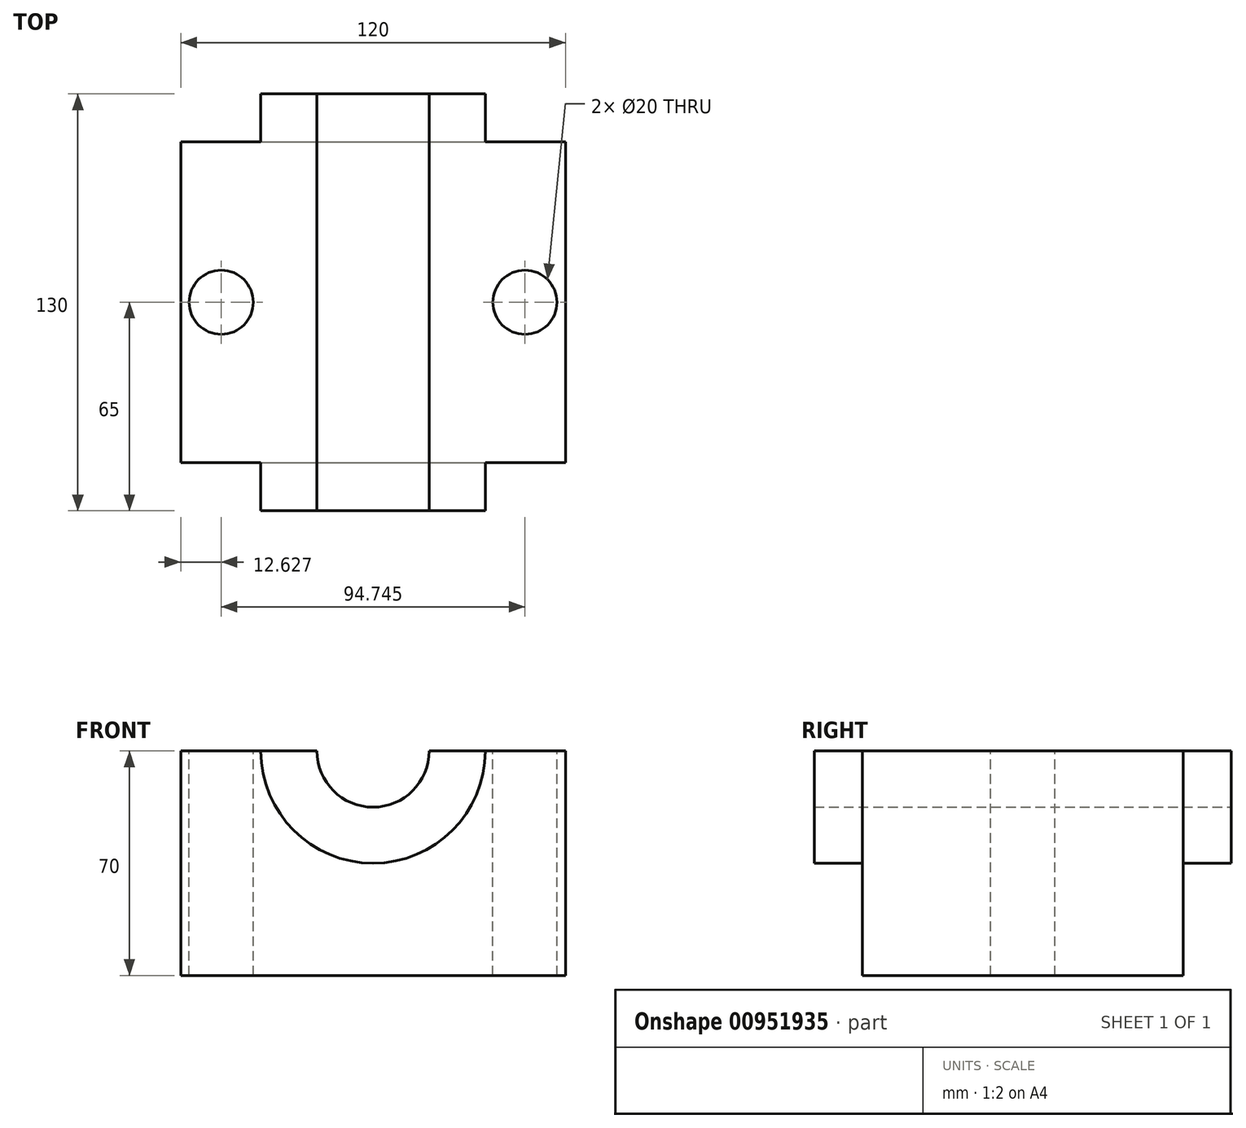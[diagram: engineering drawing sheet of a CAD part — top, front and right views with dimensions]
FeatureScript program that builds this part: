
annotation { "Feature Type Name" : "Feature", "Feature Type Description" : "" }
export const myFeature = defineFeature(function(context is Context, id is Id, definition is map)
    precondition{}
    {
        {
            var Q0;
            Q0=qCreatedBy(makeId("Front.planeOp"),FACE);
            var sketch = newSketch(context, id + "F0", { "sketchPlane" : qUnion([Q0])});
            skLineSegment(sketch, "E0.bottom", {"start": v(0, 35) * mm, "end": v(60, 35) * mm});
            skLineSegment(sketch, "E0.top", {"start": v(0, -35) * mm, "end": v(60, -35) * mm});
            skLineSegment(sketch, "E0.right", {"start": v(60, 35) * mm, "end": v(60, -35) * mm});
            skArc(sketch, "E1", {"start": v(0, 17.5) * mm, "mid": v(12.37, 22.63) * mm, "end": v(17.5, 35) * mm});
            skArc(sketch, "E2", {"start": v(0, 0) * mm, "mid": v(24.75, 10.25) * mm, "end": v(35, 35) * mm});
            skLineSegment(sketch, "E3", {"start": v(0, 35) * mm, "end": v(0, -35) * mm});
            skSolve(sketch);
        }
        {
            var Q0;
            Q0=makeQuery(id+"F0.imprint","IMPRINT",FACE,{"disambiguationData":[TD([[makeQuery(id+"F0.imprint","IMPRINT",EDGE,{"derivedFrom":sQuery(id+"F0.wireOp",EDGE,"E0.top")}),1.0]])]});
            extrude(context, id + "F1", {"entities" : qUnion([Q0]), "depth" : 50 * mm, "offsetDistance" : 25 * mm});
        }
        {
            var Q0;
            Q0=makeQuery(id+"F1.opExtrude","CAP_FACE",FACE,{"disambiguationData":[OSD([sQuery(id+"F0.wireOp",EDGE,"E0.bottom"),sQuery(id+"F0.wireOp",EDGE,"E0.top"),sQuery(id+"F0.wireOp",EDGE,"E0.left"),sQuery(id+"F0.wireOp",EDGE,"E0.right"),sQuery(id+"F0.wireOp",EDGE,"E2")])],"isStart":true});
            extrude(context, id + "F2", {"entities" : qUnion([Q0]), "operationType" : NewBodyOperationType.ADD, "depth" : 50 * mm, "offsetDistance" : 25 * mm});
        }
        {
            var Q0;
            {var subQ0=sQuery(id+"F0.wireOp",EDGE,"E1");Q0=makeQuery(id+"F0.imprint","IMPRINT",FACE,{"disambiguationData":[TD([[makeQuery(id+"F0.imprint","IMPRINT",EDGE,{"derivedFrom":subQ0}),-1.0]])]});}
            extrude(context, id + "F3", {"entities" : qUnion([Q0]), "operationType" : NewBodyOperationType.ADD, "depth" : 65 * mm, "offsetDistance" : 25 * mm});
        }
        {
            var Q0;
            Q0=makeQuery(id+"F3.opExtrude","CAP_FACE",FACE,{"disambiguationData":[OSD([sQuery(id+"F0.wireOp",EDGE,"E0.bottom"),sQuery(id+"F0.wireOp",EDGE,"E1"),sQuery(id+"F0.wireOp",EDGE,"E2")])],"isStart":true});
            extrude(context, id + "F4", {"entities" : qUnion([Q0]), "operationType" : NewBodyOperationType.ADD, "depth" : 65 * mm, "offsetDistance" : 25 * mm});
        }
        {
            var Q0;
            {var subQ0=sQuery(id+"F0.wireOp",EDGE,"E0.bottom");Q0=makeQuery(id+"F4.boolean.opBoolean","MERGE",FACE,{"derivedFrom":[makeQuery(id+"F3.boolean.opBoolean","MERGE",FACE,{"derivedFrom":[makeQuery(id+"F2.boolean.opBoolean","MERGE",FACE,{"derivedFrom":[makeQuery(id+"F1.opExtrude","SWEPT_FACE",FACE,{"disambiguationData":[OSD([subQ0])]}),makeQuery(id+"F2.opExtrude","SWEPT_FACE",FACE,{"disambiguationData":[OSD([subQ0])]})]}),makeQuery(id+"F3.opExtrude","SWEPT_FACE",FACE,{"disambiguationData":[OSD([subQ0])]})]}),makeQuery(id+"F4.opExtrude","SWEPT_FACE",FACE,{"disambiguationData":[OSD([subQ0])]})]});}
            var sketch = newSketch(context, id + "F5", { "sketchPlane" : qUnion([Q0])});
            skCircle(sketch, "E4", {"center": v(47.37, 0) * mm, "radius": 10 * mm});
            skSolve(sketch);
        }
        {
            var Q0;
            Q0=makeQuery(id+"F5.imprint","IMPRINT",FACE,{"disambiguationData":[TD([[makeQuery(id+"F5.imprint","IMPRINT",EDGE,{"derivedFrom":sQuery(id+"F5.wireOp",EDGE,"E4")}),1.0]])]});
            extrude(context, id + "F6", {"entities" : qUnion([Q0]), "operationType" : NewBodyOperationType.REMOVE, "oppositeDirection" : true, "depth" : 200 * mm, "offsetDistance" : 25 * mm});
        }
        {
            var Q0;
            Q0=makeQuery(id+"F1.opExtrude","SWEPT_BODY",BODY,{"disambiguationData":[OSD([sQuery(id+"F0.wireOp",EDGE,"E0.bottom"),sQuery(id+"F0.wireOp",EDGE,"E0.top"),sQuery(id+"F0.wireOp",EDGE,"E0.right"),sQuery(id+"F0.wireOp",EDGE,"E2"),sQuery(id+"F0.wireOp",EDGE,"E3")])]});
            var Q1;
            {var subQ0=sQuery(id+"F0.wireOp",EDGE,"E3");Q1=makeQuery(id+"F4.boolean.opBoolean","MERGE",FACE,{"derivedFrom":[makeQuery(id+"F3.boolean.opBoolean","MERGE",FACE,{"derivedFrom":[makeQuery(id+"F2.boolean.opBoolean","MERGE",FACE,{"derivedFrom":[makeQuery(id+"F1.opExtrude","SWEPT_FACE",FACE,{"disambiguationData":[OSD([subQ0])]}),makeQuery(id+"F2.opExtrude","SWEPT_FACE",FACE,{"disambiguationData":[OSD([subQ0])]})]}),makeQuery(id+"F3.opExtrude","SWEPT_FACE",FACE,{"disambiguationData":[OSD([subQ0])]})]}),makeQuery(id+"F4.opExtrude","SWEPT_FACE",FACE,{"disambiguationData":[OSD([subQ0])]})]});}
            mirror(context, id + "F7", {"operationType" : NewBodyOperationType.ADD, "entities" : qUnion([Q0]), "mirrorPlane" : qUnion([Q1])});
        }
    });
